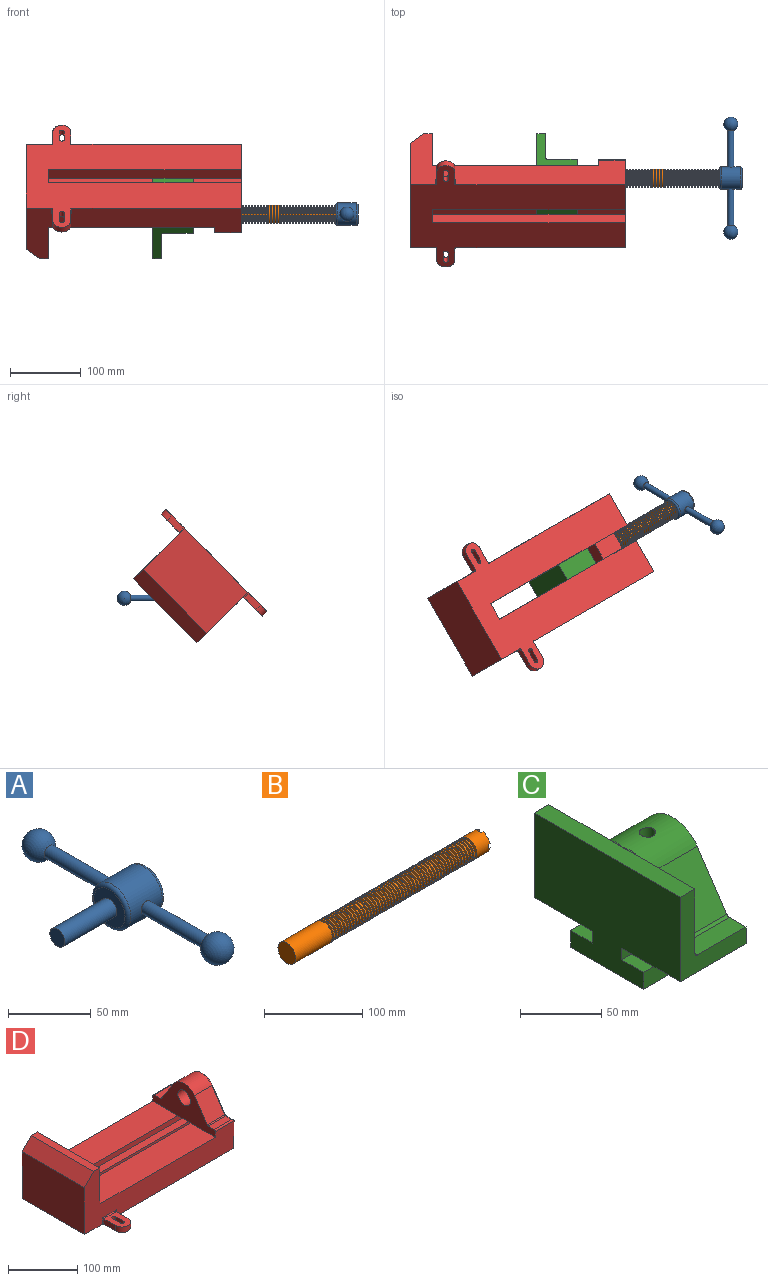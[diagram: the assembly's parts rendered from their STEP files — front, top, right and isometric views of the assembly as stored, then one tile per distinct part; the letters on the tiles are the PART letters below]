
ASSEMBLY  parts=4 mates=4
PART A: 11 faces, bbox 76.2x172.7x34.4 mm
  f0: sphere r=10.16mm, area 1231.8mm2, adj f1
  f1: cylinder r=4.45mm len=51.82mm, axis (0,1,0), area 1438.5mm2, adj f0,f4
  f2: sphere r=10.16mm, area 1231.8mm2, adj f3
  f3: cylinder r=4.45mm len=51.82mm, axis (0,1,0), area 1438.5mm2, adj f2,f4
  f4: cylinder r=15.88mm len=31.75mm, axis (-1,0,0), area 2534.7mm2, adj f1,f3,f9,f10
  f5: cylinder r=6.35mm len=44.45mm, axis (-1,0,0), area 1773.5mm2, adj f6,f8
  f6: plane 12.7x12.7mm, normal (-1,0,0), area 126.7mm2, adj f5
  f7: plane 26.67x26.67mm, normal (1,0,0), area 558.6mm2, adj f10
  f8: plane 26.67x26.67mm, normal (-1,0,0), area 432mm2, adj f5,f9
  f9: torus R=13.33mm, axis (1,0,0), area 374.8mm2, adj f4,f8
  f10: torus R=13.33mm, axis (1,0,0), area 374.8mm2, adj f4,f7
PART B: 220 faces, bbox 279.4x25.4x25.4 mm
  f0: cylinder r=12.7mm len=25.4mm, axis (-1,0,0), area 1468.2mm2, adj f1,f2,f3,f5,f7,f208,f209,f210
  f1: plane 9.9x9.9mm, normal (1,0,0), area 62.3mm2, adj f0,f4,f213,f216
  f2: plane 9.9x9.9mm, normal (1,0,0), area 62.3mm2, adj f0,f4,f210,f218
  f3: plane 9.9x9.9mm, normal (1,0,0), area 62.3mm2, adj f0,f4,f209,f212
  f4: cylinder r=6.35mm len=25.4mm, axis (1,0,0), area 960.3mm2, adj f1,f2,f3,f5,f6,f208,f209,f210
  f5: plane 9.9x9.9mm, normal (1,0,0), area 62.3mm2, adj f0,f4,f215,f217
  f6: plane 12.7x12.7mm, normal (1,0,0), area 126.7mm2, adj f4
  f7: cone r=12.7mm half-angle=76deg, axis (1,0,0), area 188mm2, adj f0,f9
  f8: cone r=10.16mm half-angle=76deg, axis (-1,0,0), area 188mm2, adj f9,f10
  f9: cylinder r=10.16mm len=20.32mm, axis (1,0,0), area 81.1mm2, adj f7,f8
  f10: cylinder r=12.7mm len=25.4mm, axis (-1,0,0), area 131.7mm2, adj f8,f11
  f11: cone r=12.7mm half-angle=76deg, axis (1,0,0), area 188mm2, adj f10,f13
  f12: cone r=10.16mm half-angle=76deg, axis (-1,0,0), area 188mm2, adj f13,f14
  f13: cylinder r=10.16mm len=20.32mm, axis (1,0,0), area 81.1mm2, adj f11,f12
  f14: cylinder r=12.7mm len=25.4mm, axis (-1,0,0), area 131.7mm2, adj f12,f15
  f15: cone r=12.7mm half-angle=76deg, axis (1,0,0), area 188mm2, adj f14,f17
  f16: cone r=10.16mm half-angle=76deg, axis (-1,0,0), area 188mm2, adj f17,f18
  f17: cylinder r=10.16mm len=20.32mm, axis (1,0,0), area 81.1mm2, adj f15,f16
  f18: cylinder r=12.7mm len=25.4mm, axis (-1,0,0), area 131.7mm2, adj f16,f19
  f19: cone r=12.7mm half-angle=76deg, axis (1,0,0), area 188mm2, adj f18,f21
  f20: cone r=10.16mm half-angle=76deg, axis (-1,0,0), area 188mm2, adj f21,f22
  f21: cylinder r=10.16mm len=20.32mm, axis (1,0,0), area 81.1mm2, adj f19,f20
  f22: cylinder r=12.7mm len=25.4mm, axis (-1,0,0), area 131.7mm2, adj f20,f23
  f23: cone r=12.7mm half-angle=76deg, axis (1,0,0), area 188mm2, adj f22,f25
  f24: cone r=10.16mm half-angle=76deg, axis (-1,0,0), area 188mm2, adj f25,f26
  f25: cylinder r=10.16mm len=20.32mm, axis (1,0,0), area 81.1mm2, adj f23,f24
  f26: cylinder r=12.7mm len=25.4mm, axis (-1,0,0), area 131.7mm2, adj f24,f27
  f27: cone r=12.7mm half-angle=76deg, axis (1,0,0), area 188mm2, adj f26,f29
  f28: cone r=10.16mm half-angle=76deg, axis (-1,0,0), area 188mm2, adj f29,f30
  f29: cylinder r=10.16mm len=20.32mm, axis (1,0,0), area 81.1mm2, adj f27,f28
  f30: cylinder r=12.7mm len=25.4mm, axis (-1,0,0), area 131.7mm2, adj f28,f31
  f31: cone r=12.7mm half-angle=76deg, axis (1,0,0), area 188mm2, adj f30,f33
  f32: cone r=10.16mm half-angle=76deg, axis (-1,0,0), area 188mm2, adj f33,f34
  f33: cylinder r=10.16mm len=20.32mm, axis (1,0,0), area 81.1mm2, adj f31,f32
  f34: cylinder r=12.7mm len=25.4mm, axis (-1,0,0), area 131.7mm2, adj f32,f35
  f35: cone r=12.7mm half-angle=76deg, axis (1,0,0), area 188mm2, adj f34,f37
  f36: cone r=10.16mm half-angle=76deg, axis (-1,0,0), area 188mm2, adj f37,f38
  f37: cylinder r=10.16mm len=20.32mm, axis (1,0,0), area 81.1mm2, adj f35,f36
  f38: cylinder r=12.7mm len=25.4mm, axis (-1,0,0), area 131.7mm2, adj f36,f39
  f39: cone r=12.7mm half-angle=76deg, axis (1,0,0), area 188mm2, adj f38,f41
  f40: cone r=10.16mm half-angle=76deg, axis (-1,0,0), area 188mm2, adj f41,f42
  f41: cylinder r=10.16mm len=20.32mm, axis (1,0,0), area 81.1mm2, adj f39,f40
  f42: cylinder r=12.7mm len=25.4mm, axis (-1,0,0), area 131.7mm2, adj f40,f43
  f43: cone r=12.7mm half-angle=76deg, axis (1,0,0), area 188mm2, adj f42,f45
  f44: cone r=10.16mm half-angle=76deg, axis (-1,0,0), area 188mm2, adj f45,f46
  f45: cylinder r=10.16mm len=20.32mm, axis (1,0,0), area 81.1mm2, adj f43,f44
  f46: cylinder r=12.7mm len=25.4mm, axis (-1,0,0), area 131.7mm2, adj f44,f47
  f47: cone r=12.7mm half-angle=76deg, axis (1,0,0), area 188mm2, adj f46,f49
  f48: cone r=10.16mm half-angle=76deg, axis (-1,0,0), area 188mm2, adj f49,f50
  f49: cylinder r=10.16mm len=20.32mm, axis (1,0,0), area 81.1mm2, adj f47,f48
  f50: cylinder r=12.7mm len=25.4mm, axis (-1,0,0), area 131.7mm2, adj f48,f51
  f51: cone r=12.7mm half-angle=76deg, axis (1,0,0), area 188mm2, adj f50,f53
  f52: cone r=10.16mm half-angle=76deg, axis (-1,0,0), area 188mm2, adj f53,f54
  f53: cylinder r=10.16mm len=20.32mm, axis (1,0,0), area 81.1mm2, adj f51,f52
  f54: cylinder r=12.7mm len=25.4mm, axis (-1,0,0), area 131.7mm2, adj f52,f55
  f55: cone r=12.7mm half-angle=76deg, axis (1,0,0), area 188mm2, adj f54,f57
  f56: cone r=10.16mm half-angle=76deg, axis (-1,0,0), area 188mm2, adj f57,f58
  f57: cylinder r=10.16mm len=20.32mm, axis (1,0,0), area 81.1mm2, adj f55,f56
  f58: cylinder r=12.7mm len=25.4mm, axis (-1,0,0), area 131.7mm2, adj f56,f59
  f59: cone r=12.7mm half-angle=76deg, axis (1,0,0), area 188mm2, adj f58,f61
  f60: cone r=10.16mm half-angle=76deg, axis (-1,0,0), area 188mm2, adj f61,f62
  f61: cylinder r=10.16mm len=20.32mm, axis (1,0,0), area 81.1mm2, adj f59,f60
  f62: cylinder r=12.7mm len=25.4mm, axis (-1,0,0), area 131.7mm2, adj f60,f63
  f63: cone r=12.7mm half-angle=76deg, axis (1,0,0), area 188mm2, adj f62,f65
  f64: cone r=10.16mm half-angle=76deg, axis (-1,0,0), area 188mm2, adj f65,f66
  f65: cylinder r=10.16mm len=20.32mm, axis (1,0,0), area 81.1mm2, adj f63,f64
  f66: cylinder r=12.7mm len=25.4mm, axis (-1,0,0), area 131.7mm2, adj f64,f67
  f67: cone r=12.7mm half-angle=76deg, axis (1,0,0), area 188mm2, adj f66,f69
  f68: cone r=10.16mm half-angle=76deg, axis (-1,0,0), area 188mm2, adj f69,f70
  f69: cylinder r=10.16mm len=20.32mm, axis (1,0,0), area 81.1mm2, adj f67,f68
  f70: cylinder r=12.7mm len=25.4mm, axis (-1,0,0), area 131.7mm2, adj f68,f71
  f71: cone r=12.7mm half-angle=76deg, axis (1,0,0), area 188mm2, adj f70,f73
  f72: cone r=10.16mm half-angle=76deg, axis (-1,0,0), area 188mm2, adj f73,f74
  f73: cylinder r=10.16mm len=20.32mm, axis (1,0,0), area 81.1mm2, adj f71,f72
  f74: cylinder r=12.7mm len=25.4mm, axis (-1,0,0), area 131.7mm2, adj f72,f75
  f75: cone r=12.7mm half-angle=76deg, axis (1,0,0), area 188mm2, adj f74,f77
  f76: cone r=10.16mm half-angle=76deg, axis (-1,0,0), area 188mm2, adj f77,f78
  f77: cylinder r=10.16mm len=20.32mm, axis (1,0,0), area 81.1mm2, adj f75,f76
  f78: cylinder r=12.7mm len=25.4mm, axis (-1,0,0), area 131.7mm2, adj f76,f79
  f79: cone r=12.7mm half-angle=76deg, axis (1,0,0), area 188mm2, adj f78,f81
  f80: cone r=10.16mm half-angle=76deg, axis (-1,0,0), area 188mm2, adj f81,f82
  f81: cylinder r=10.16mm len=20.32mm, axis (1,0,0), area 81.1mm2, adj f79,f80
  f82: cylinder r=12.7mm len=25.4mm, axis (-1,0,0), area 131.7mm2, adj f80,f83
  f83: cone r=12.7mm half-angle=76deg, axis (1,0,0), area 188mm2, adj f82,f85
  f84: cone r=10.16mm half-angle=76deg, axis (-1,0,0), area 188mm2, adj f85,f86
  f85: cylinder r=10.16mm len=20.32mm, axis (1,0,0), area 81.1mm2, adj f83,f84
  f86: cylinder r=12.7mm len=25.4mm, axis (-1,0,0), area 131.7mm2, adj f84,f87
  f87: cone r=12.7mm half-angle=76deg, axis (1,0,0), area 188mm2, adj f86,f89
  f88: cone r=10.16mm half-angle=76deg, axis (-1,0,0), area 188mm2, adj f89,f90
  f89: cylinder r=10.16mm len=20.32mm, axis (1,0,0), area 81.1mm2, adj f87,f88
  f90: cylinder r=12.7mm len=25.4mm, axis (-1,0,0), area 131.7mm2, adj f88,f91
  f91: cone r=12.7mm half-angle=76deg, axis (1,0,0), area 188mm2, adj f90,f93
  f92: cone r=10.16mm half-angle=76deg, axis (-1,0,0), area 188mm2, adj f93,f94
  f93: cylinder r=10.16mm len=20.32mm, axis (1,0,0), area 81.1mm2, adj f91,f92
  f94: cylinder r=12.7mm len=25.4mm, axis (-1,0,0), area 131.7mm2, adj f92,f95
  f95: cone r=12.7mm half-angle=76deg, axis (1,0,0), area 188mm2, adj f94,f97
  f96: cone r=10.16mm half-angle=76deg, axis (-1,0,0), area 188mm2, adj f97,f98
  f97: cylinder r=10.16mm len=20.32mm, axis (1,0,0), area 81.1mm2, adj f95,f96
  f98: cylinder r=12.7mm len=25.4mm, axis (-1,0,0), area 131.7mm2, adj f96,f99
  f99: cone r=12.7mm half-angle=76deg, axis (1,0,0), area 188mm2, adj f98,f101
  f100: cone r=10.16mm half-angle=76deg, axis (-1,0,0), area 188mm2, adj f101,f102
  f101: cylinder r=10.16mm len=20.32mm, axis (1,0,0), area 81.1mm2, adj f99,f100
  f102: cylinder r=12.7mm len=25.4mm, axis (-1,0,0), area 131.7mm2, adj f100,f103
  f103: cone r=12.7mm half-angle=76deg, axis (1,0,0), area 188mm2, adj f102,f105
  f104: cone r=10.16mm half-angle=76deg, axis (-1,0,0), area 188mm2, adj f105,f106
  f105: cylinder r=10.16mm len=20.32mm, axis (1,0,0), area 81.1mm2, adj f103,f104
  f106: cylinder r=12.7mm len=25.4mm, axis (-1,0,0), area 131.7mm2, adj f104,f107
  f107: cone r=12.7mm half-angle=76deg, axis (1,0,0), area 188mm2, adj f106,f109
  f108: cone r=10.16mm half-angle=76deg, axis (-1,0,0), area 188mm2, adj f109,f110
  f109: cylinder r=10.16mm len=20.32mm, axis (1,0,0), area 81.1mm2, adj f107,f108
  f110: cylinder r=12.7mm len=25.4mm, axis (-1,0,0), area 131.7mm2, adj f108,f111
  f111: cone r=12.7mm half-angle=76deg, axis (1,0,0), area 188mm2, adj f110,f113
  f112: cone r=10.16mm half-angle=76deg, axis (-1,0,0), area 188mm2, adj f113,f114
  f113: cylinder r=10.16mm len=20.32mm, axis (1,0,0), area 81.1mm2, adj f111,f112
  f114: cylinder r=12.7mm len=25.4mm, axis (-1,0,0), area 131.7mm2, adj f112,f115
  f115: cone r=12.7mm half-angle=76deg, axis (1,0,0), area 188mm2, adj f114,f117
  f116: cone r=10.16mm half-angle=76deg, axis (-1,0,0), area 188mm2, adj f117,f118
  f117: cylinder r=10.16mm len=20.32mm, axis (1,0,0), area 81.1mm2, adj f115,f116
  f118: cylinder r=12.7mm len=25.4mm, axis (-1,0,0), area 131.7mm2, adj f116,f119
  f119: cone r=12.7mm half-angle=76deg, axis (1,0,0), area 188mm2, adj f118,f121
  f120: cone r=10.16mm half-angle=76deg, axis (-1,0,0), area 188mm2, adj f121,f122
  f121: cylinder r=10.16mm len=20.32mm, axis (1,0,0), area 81.1mm2, adj f119,f120
  f122: cylinder r=12.7mm len=25.4mm, axis (-1,0,0), area 131.7mm2, adj f120,f123
  f123: cone r=12.7mm half-angle=76deg, axis (1,0,0), area 188mm2, adj f122,f125
  f124: cone r=10.16mm half-angle=76deg, axis (-1,0,0), area 188mm2, adj f125,f126
  f125: cylinder r=10.16mm len=20.32mm, axis (1,0,0), area 81.1mm2, adj f123,f124
  f126: cylinder r=12.7mm len=25.4mm, axis (-1,0,0), area 131.7mm2, adj f124,f127
  f127: cone r=12.7mm half-angle=76deg, axis (1,0,0), area 188mm2, adj f126,f129
  f128: cone r=10.16mm half-angle=76deg, axis (-1,0,0), area 188mm2, adj f129,f130
  f129: cylinder r=10.16mm len=20.32mm, axis (1,0,0), area 81.1mm2, adj f127,f128
  f130: cylinder r=12.7mm len=25.4mm, axis (-1,0,0), area 131.7mm2, adj f128,f131
  f131: cone r=12.7mm half-angle=76deg, axis (1,0,0), area 188mm2, adj f130,f133
  f132: cone r=10.16mm half-angle=76deg, axis (-1,0,0), area 188mm2, adj f133,f134
  f133: cylinder r=10.16mm len=20.32mm, axis (1,0,0), area 81.1mm2, adj f131,f132
  f134: cylinder r=12.7mm len=25.4mm, axis (-1,0,0), area 131.7mm2, adj f132,f135
  f135: cone r=12.7mm half-angle=76deg, axis (1,0,0), area 188mm2, adj f134,f137
  f136: cone r=10.16mm half-angle=76deg, axis (-1,0,0), area 188mm2, adj f137,f138
  f137: cylinder r=10.16mm len=20.32mm, axis (1,0,0), area 81.1mm2, adj f135,f136
  f138: cylinder r=12.7mm len=25.4mm, axis (-1,0,0), area 131.7mm2, adj f136,f139
  f139: cone r=12.7mm half-angle=76deg, axis (1,0,0), area 188mm2, adj f138,f141
  f140: cone r=10.16mm half-angle=76deg, axis (-1,0,0), area 188mm2, adj f141,f142
  f141: cylinder r=10.16mm len=20.32mm, axis (1,0,0), area 81.1mm2, adj f139,f140
  f142: cylinder r=12.7mm len=25.4mm, axis (-1,0,0), area 131.7mm2, adj f140,f143
  f143: cone r=12.7mm half-angle=76deg, axis (1,0,0), area 188mm2, adj f142,f145
  f144: cone r=10.16mm half-angle=76deg, axis (-1,0,0), area 188mm2, adj f145,f146
  f145: cylinder r=10.16mm len=20.32mm, axis (1,0,0), area 81.1mm2, adj f143,f144
  f146: cylinder r=12.7mm len=25.4mm, axis (-1,0,0), area 131.7mm2, adj f144,f147
  f147: cone r=12.7mm half-angle=76deg, axis (1,0,0), area 188mm2, adj f146,f149
  f148: cone r=10.16mm half-angle=76deg, axis (-1,0,0), area 188mm2, adj f149,f150
  f149: cylinder r=10.16mm len=20.32mm, axis (1,0,0), area 81.1mm2, adj f147,f148
  f150: cylinder r=12.7mm len=25.4mm, axis (-1,0,0), area 131.7mm2, adj f148,f151
  f151: cone r=12.7mm half-angle=76deg, axis (1,0,0), area 188mm2, adj f150,f153
  f152: cone r=10.16mm half-angle=76deg, axis (-1,0,0), area 188mm2, adj f153,f154
  f153: cylinder r=10.16mm len=20.32mm, axis (1,0,0), area 81.1mm2, adj f151,f152
  f154: cylinder r=12.7mm len=25.4mm, axis (-1,0,0), area 131.7mm2, adj f152,f155
  f155: cone r=12.7mm half-angle=76deg, axis (1,0,0), area 188mm2, adj f154,f157
  f156: cone r=10.16mm half-angle=76deg, axis (-1,0,0), area 188mm2, adj f157,f158
  f157: cylinder r=10.16mm len=20.32mm, axis (1,0,0), area 81.1mm2, adj f155,f156
  f158: cylinder r=12.7mm len=25.4mm, axis (-1,0,0), area 131.7mm2, adj f156,f159
  f159: cone r=12.7mm half-angle=76deg, axis (1,0,0), area 188mm2, adj f158,f161
  f160: cone r=10.16mm half-angle=76deg, axis (-1,0,0), area 188mm2, adj f161,f162
  f161: cylinder r=10.16mm len=20.32mm, axis (1,0,0), area 81.1mm2, adj f159,f160
  f162: cylinder r=12.7mm len=25.4mm, axis (-1,0,0), area 131.7mm2, adj f160,f163
  f163: cone r=12.7mm half-angle=76deg, axis (1,0,0), area 188mm2, adj f162,f165
  f164: cone r=10.16mm half-angle=76deg, axis (-1,0,0), area 188mm2, adj f165,f166
  f165: cylinder r=10.16mm len=20.32mm, axis (1,0,0), area 81.1mm2, adj f163,f164
  f166: cylinder r=12.7mm len=25.4mm, axis (-1,0,0), area 131.7mm2, adj f164,f167
  f167: cone r=12.7mm half-angle=76deg, axis (1,0,0), area 188mm2, adj f166,f169
  f168: cone r=10.16mm half-angle=76deg, axis (-1,0,0), area 188mm2, adj f169,f170
  f169: cylinder r=10.16mm len=20.32mm, axis (1,0,0), area 81.1mm2, adj f167,f168
  f170: cylinder r=12.7mm len=25.4mm, axis (-1,0,0), area 131.7mm2, adj f168,f171
  f171: cone r=12.7mm half-angle=76deg, axis (1,0,0), area 188mm2, adj f170,f173
  f172: cone r=10.16mm half-angle=76deg, axis (-1,0,0), area 188mm2, adj f173,f174
  f173: cylinder r=10.16mm len=20.32mm, axis (1,0,0), area 81.1mm2, adj f171,f172
  f174: cylinder r=12.7mm len=25.4mm, axis (-1,0,0), area 131.7mm2, adj f172,f175
  f175: cone r=12.7mm half-angle=76deg, axis (1,0,0), area 188mm2, adj f174,f177
  f176: cone r=10.16mm half-angle=76deg, axis (-1,0,0), area 188mm2, adj f177,f178
  f177: cylinder r=10.16mm len=20.32mm, axis (1,0,0), area 81.1mm2, adj f175,f176
  f178: cylinder r=12.7mm len=25.4mm, axis (-1,0,0), area 131.7mm2, adj f176,f179
  f179: cone r=12.7mm half-angle=76deg, axis (1,0,0), area 188mm2, adj f178,f181
  f180: cone r=10.16mm half-angle=76deg, axis (-1,0,0), area 188mm2, adj f181,f182
  f181: cylinder r=10.16mm len=20.32mm, axis (1,0,0), area 81.1mm2, adj f179,f180
  f182: cylinder r=12.7mm len=25.4mm, axis (-1,0,0), area 131.7mm2, adj f180,f183
  f183: cone r=12.7mm half-angle=76deg, axis (1,0,0), area 188mm2, adj f182,f185
  f184: cone r=10.16mm half-angle=76deg, axis (-1,0,0), area 188mm2, adj f185,f186
  f185: cylinder r=10.16mm len=20.32mm, axis (1,0,0), area 81.1mm2, adj f183,f184
  f186: cylinder r=12.7mm len=25.4mm, axis (-1,0,0), area 131.7mm2, adj f184,f187
  f187: cone r=12.7mm half-angle=76deg, axis (1,0,0), area 188mm2, adj f186,f189
  f188: cone r=10.16mm half-angle=76deg, axis (-1,0,0), area 188mm2, adj f189,f190
  f189: cylinder r=10.16mm len=20.32mm, axis (1,0,0), area 81.1mm2, adj f187,f188
  f190: cylinder r=12.7mm len=25.4mm, axis (-1,0,0), area 131.7mm2, adj f188,f191
  f191: cone r=12.7mm half-angle=76deg, axis (1,0,0), area 188mm2, adj f190,f193
  f192: cone r=10.16mm half-angle=76deg, axis (-1,0,0), area 188mm2, adj f193,f194
  f193: cylinder r=10.16mm len=20.32mm, axis (1,0,0), area 81.1mm2, adj f191,f192
  f194: cylinder r=12.7mm len=25.4mm, axis (-1,0,0), area 131.7mm2, adj f192,f195
  f195: cone r=12.7mm half-angle=76deg, axis (1,0,0), area 188mm2, adj f194,f197
  f196: cone r=10.16mm half-angle=76deg, axis (-1,0,0), area 188mm2, adj f197,f198
  f197: cylinder r=10.16mm len=20.32mm, axis (1,0,0), area 81.1mm2, adj f195,f196
  f198: cylinder r=12.7mm len=25.4mm, axis (-1,0,0), area 131.7mm2, adj f196,f199
  f199: cone r=12.7mm half-angle=76deg, axis (1,0,0), area 188mm2, adj f198,f201
  f200: cone r=10.16mm half-angle=76deg, axis (-1,0,0), area 188mm2, adj f201,f202
  f201: cylinder r=10.16mm len=20.32mm, axis (1,0,0), area 81.1mm2, adj f199,f200
  f202: cylinder r=12.7mm len=25.4mm, axis (-1,0,0), area 131.7mm2, adj f200,f203
  f203: cone r=12.7mm half-angle=76deg, axis (1,0,0), area 188mm2, adj f202,f205
  f204: cone r=10.16mm half-angle=76deg, axis (-1,0,0), area 188mm2, adj f205,f207
  f205: cylinder r=10.16mm len=20.32mm, axis (1,0,0), area 81.1mm2, adj f203,f204
  f206: plane 25.4x25.4mm, normal (-1,0,0), area 506.7mm2, adj f207
  f207: cylinder r=12.7mm len=52.45mm, axis (-1,0,0), area 4185.4mm2, adj f204,f206
  f208: plane 6.88x5.08mm, normal (1,0,0), area 32.7mm2, adj f0,f4,f209,f210
  f209: plane 6.62x2.54mm, normal (0,-1,0), area 16.8mm2, adj f0,f3,f4,f208
  f210: plane 6.62x2.54mm, normal (0,1,0), area 16.8mm2, adj f0,f2,f4,f208
  f211: plane 6.88x5.08mm, normal (1,0,0), area 32.7mm2, adj f0,f4,f212,f213
  f212: plane 6.62x2.54mm, normal (0,0,1), area 16.8mm2, adj f0,f3,f4,f211
  f213: plane 6.62x2.54mm, normal (0,0,-1), area 16.8mm2, adj f0,f1,f4,f211
  f214: plane 6.88x5.08mm, normal (1,0,0), area 32.7mm2, adj f0,f4,f215,f216
  f215: plane 6.62x2.54mm, normal (0,1,0), area 16.8mm2, adj f0,f4,f5,f214
  f216: plane 6.62x2.54mm, normal (0,-1,0), area 16.8mm2, adj f0,f1,f4,f214
  f217: plane 6.62x2.54mm, normal (0,0,-1), area 16.8mm2, adj f0,f4,f5,f219
  f218: plane 6.62x2.54mm, normal (0,0,1), area 16.8mm2, adj f0,f2,f4,f219
  f219: plane 6.88x5.08mm, normal (1,0,0), area 32.7mm2, adj f0,f4,f217,f218
PART C: 36 faces, bbox 57.2x127x89 mm
  f0: plane 57.15x50.8mm, normal (0,0,-1), area 2903.2mm2, adj f6,f9,f10,f23
  f1: cylinder r=12.7mm len=44.45mm, axis (1,0,0), area 3464.3mm2, adj f6,f15,f16
  f2: plane 41.91x14.52mm, normal (0,0,1), area 608.5mm2, adj f6,f11,f24,f25
  f3: plane 51.86x48.26mm, normal (1,0,0), area 1495.7mm2, adj f8,f10,f31,f33,f35
  f4: plane 51.86x48.26mm, normal (1,0,0), area 1495.7mm2, adj f8,f11,f24,f28,f29
  f5: plane 57.15x50.8mm, normal (0,0,-1), area 2903.2mm2, adj f6,f9,f11,f22
  f6: plane 127x85.09mm, normal (1,0,0), area 5190.6mm2, adj f0,f1,f2,f5,f7,f10,f11,f12
  f7: plane 41.91x14.52mm, normal (0,0,1), area 608.5mm2, adj f6,f10,f30,f31
  f8: plane 127x12.7mm, normal (0,0,1), area 1612.9mm2, adj f3,f4,f9,f10,f11,f26,f34
  f9: plane 127x85.09mm, normal (-1,0,0), area 9096.8mm2, adj f0,f5,f8,f10,f11,f17,f18,f19
  f10: plane 63.5x57.15mm, normal (0,-1,0), area 1372.3mm2, adj f0,f3,f6,f7,f8,f9,f31
  f11: plane 63.5x57.15mm, normal (0,1,0), area 1372.3mm2, adj f2,f4,f5,f6,f8,f9,f24
  f12: plane 41.91x38.43mm, normal (0,-0.83,0.56), area 1939.2mm2, adj f6,f13,f30,f33
  f13: cylinder r=25.4mm len=44.45mm, axis (1,0,0), area 2026.5mm2, adj f6,f12,f14,f16,f26,f28,f34,f35
  f14: plane 41.91x38.43mm, normal (0,0.83,0.56), area 1939.2mm2, adj f6,f13,f25,f29
  f15: plane 25.4x25.4mm, normal (1,0,0), area 506.7mm2, adj f1
  f16: cylinder r=5.08mm len=13.76mm, axis (0,0,1), area 414mm2, adj f1,f13
  f17: plane 57.15x19.05mm, normal (0,0,1), area 1088.7mm2, adj f6,f9,f18,f23
  f18: plane 57.15x12.7mm, normal (0,-1,0), area 725.8mm2, adj f6,f9,f17,f19
  f19: plane 63.5x57.15mm, normal (0,0,-1), area 3629mm2, adj f6,f9,f18,f20
  f20: plane 57.15x12.7mm, normal (0,1,0), area 725.8mm2, adj f6,f9,f19,f21
  f21: plane 57.15x19.05mm, normal (0,0,1), area 1088.7mm2, adj f6,f9,f20,f22
  f22: plane 57.15x8.89mm, normal (0,1,0), area 508.1mm2, adj f5,f6,f9,f21
  f23: plane 57.15x8.89mm, normal (0,-1,0), area 508.1mm2, adj f0,f6,f9,f17
  f24: cylinder r=2.54mm len=14.52mm, axis (0,-1,0), area 57.9mm2, adj f2,f4,f11,f27
  f25: cylinder r=2.54mm len=41.91mm, axis (1,0,0), area 104.3mm2, adj f2,f6,f14,f27
  f26: bspline ~12.24x2.8mm, area 20.9mm2, adj f8,f13,f28
  f27: sphere r=2.54mm, area 6.3mm2, adj f24,f25,f29
  f28: torus R=27.94mm, axis (1,0,0), area 57.8mm2, adj f4,f13,f26,f29
  f29: cylinder r=2.54mm len=39.84mm, axis (0,-0.56,0.83), area 184.6mm2, adj f4,f14,f27,f28
  f30: cylinder r=2.54mm len=41.91mm, axis (1,0,0), area 104.3mm2, adj f6,f7,f12,f32
  f31: cylinder r=2.54mm len=14.52mm, axis (0,-1,0), area 57.9mm2, adj f3,f7,f10,f32
  f32: sphere r=2.54mm, area 6.3mm2, adj f30,f31,f33
  f33: cylinder r=2.54mm len=39.84mm, axis (0,-0.56,-0.83), area 184.6mm2, adj f3,f12,f32,f35
  f34: bspline ~12.24x2.8mm, area 20.9mm2, adj f8,f13,f35
  f35: torus R=27.94mm, axis (1,0,0), area 57.8mm2, adj f3,f13,f33,f34
PART D: 61 faces, bbox 304.8x203.2x103.7 mm
  f0: plane 304.8x101.6mm, normal (0,1,0), area 13520.3mm2, adj f3,f4,f5,f6,f7,f8,f9,f16
  f1: plane 304.8x101.6mm, normal (0,-1,0), area 13520.3mm2, adj f2,f3,f5,f6,f7,f8,f9,f16
  f2: plane 234.95x50.8mm, normal (0,0,1), area 11935.5mm2, adj f1,f5,f16,f26
  f3: plane 127x99.06mm, normal (1,0,0), area 7097.5mm2, adj f0,f1,f9,f14,f17,f18,f19,f20
  f4: plane 234.95x50.8mm, normal (0,0,1), area 11935.5mm2, adj f0,f5,f16,f27
  f5: plane 127x101.6mm, normal (1,0,0), area 9516.1mm2, adj f0,f1,f2,f4,f6,f9,f18,f19
  f6: plane 127x12.7mm, normal (0,0,1), area 1612.9mm2, adj f0,f1,f5,f7
  f7: plane 127x19.05mm, normal (-0.71,0,0.71), area 3421.5mm2, adj f0,f1,f6,f8
  f8: plane 127x82.55mm, normal (-1,0,0), area 10483.8mm2, adj f0,f1,f7,f9
  f9: plane 304.8x203.2mm, normal (0,0,-1), area 33298.3mm2, adj f0,f1,f3,f5,f8,f21,f22,f39
  f10: plane 35.56x11.98mm, normal (0,0,1), area 426mm2, adj f16,f28,f29,f30
  f11: plane 38.43x35.56mm, normal (0,0.83,0.56), area 1645.4mm2, adj f12,f16,f29,f32
  f12: cylinder r=25.4mm len=42.19mm, axis (1,0,0), area 1770.2mm2, adj f11,f13,f16,f33
  f13: plane 38.43x35.56mm, normal (0,-0.83,0.56), area 1645.4mm2, adj f12,f16,f34,f35
  f14: cylinder r=12.7mm len=38.1mm, axis (1,0,0), area 3040.2mm2, adj f3,f16
  f15: plane 35.56x11.98mm, normal (0,0,1), area 426mm2, adj f16,f34,f36,f38
  f16: plane 127x63.5mm, normal (-1,0,0), area 4155.5mm2, adj f0,f1,f2,f4,f10,f11,f12,f13
  f17: plane 38.1x25.4mm, normal (0,0,-1), area 967.7mm2, adj f3,f16,f26,f27
  f18: plane 273.05x19.05mm, normal (0,0,-1), area 5201.6mm2, adj f3,f5,f19,f26
  f19: plane 273.05x12.7mm, normal (0,1,0), area 3467.7mm2, adj f3,f5,f18,f20
  f20: plane 273.05x19.05mm, normal (0,0,1), area 5201.6mm2, adj f3,f5,f19,f21
  f21: plane 273.05x16.51mm, normal (0,1,0), area 4508.1mm2, adj f3,f5,f9,f20
  f22: plane 273.05x16.51mm, normal (0,-1,0), area 4508.1mm2, adj f3,f5,f9,f23
  f23: plane 273.05x19.05mm, normal (0,0,1), area 5201.6mm2, adj f3,f5,f22,f24
  f24: plane 273.05x12.7mm, normal (0,-1,0), area 3467.7mm2, adj f3,f5,f23,f25
  f25: plane 273.05x19.05mm, normal (0,0,-1), area 5201.6mm2, adj f3,f5,f24,f27
  f26: plane 273.05x8.89mm, normal (0,1,0), area 2427.4mm2, adj f2,f3,f5,f17,f18
  f27: plane 273.05x8.89mm, normal (0,-1,0), area 2427.4mm2, adj f3,f4,f5,f17,f25
  f28: cylinder r=2.54mm len=38.1mm, axis (1,0,0), area 148.3mm2, adj f0,f10,f16,f30
  f29: cylinder r=2.54mm len=35.56mm, axis (-1,0,0), area 88.5mm2, adj f10,f11,f16,f31
  f30: cylinder r=2.54mm len=14.52mm, axis (0,1,0), area 54.3mm2, adj f3,f10,f28,f31
  f31: torus R=5.08mm, axis (-1,0,0), area 13.5mm2, adj f3,f29,f30,f32
  f32: cylinder r=2.54mm len=39.84mm, axis (0,0.56,-0.83), area 184.6mm2, adj f3,f11,f31,f33
  f33: torus R=22.86mm, axis (-1,0,0), area 191.4mm2, adj f3,f12,f32,f35
  f34: cylinder r=2.54mm len=35.56mm, axis (-1,0,0), area 88.5mm2, adj f13,f15,f16,f37
  f35: cylinder r=2.54mm len=39.84mm, axis (0,0.56,0.83), area 184.6mm2, adj f3,f13,f33,f37
  f36: cylinder r=2.54mm len=38.1mm, axis (-1,0,0), area 148.3mm2, adj f1,f15,f16,f38
  f37: torus R=5.08mm, axis (-1,0,0), area 13.5mm2, adj f3,f34,f35,f38
  f38: cylinder r=2.54mm len=14.52mm, axis (0,1,0), area 54.3mm2, adj f3,f15,f36,f37
  f39: plane 23.88x9.53mm, normal (-1,0,0), area 227.4mm2, adj f9,f45,f46,f60
  f40: plane 23.88x9.53mm, normal (1,0,0), area 227.4mm2, adj f9,f45,f46,f58
  f41: cylinder r=3.3mm len=9.53mm, axis (0,0,-1), area 98.8mm2, adj f9,f42,f44,f46
  f42: plane 15.62x9.53mm, normal (-1,0,0), area 148.8mm2, adj f9,f41,f43,f46
  f43: cylinder r=3.3mm len=9.53mm, axis (0,0,-1), area 98.8mm2, adj f9,f42,f44,f46
  f44: plane 15.62x9.53mm, normal (1,0,0), area 148.8mm2, adj f9,f41,f43,f46
  f45: cylinder r=12.7mm len=25.4mm, axis (0,0,-1), area 380mm2, adj f9,f39,f40,f46
  f46: plane 36.58x25.4mm, normal (0,0,1), area 722.4mm2, adj f39,f40,f41,f42,f43,f44,f45,f59
  f47: plane 23.88x9.53mm, normal (-1,0,0), area 227.4mm2, adj f9,f53,f54,f56
  f48: plane 23.88x9.53mm, normal (1,0,0), area 227.4mm2, adj f9,f53,f54,f55
  f49: cylinder r=3.3mm len=9.53mm, axis (0,0,-1), area 98.8mm2, adj f9,f50,f52,f54
  f50: plane 15.62x9.53mm, normal (-1,0,0), area 148.8mm2, adj f9,f49,f51,f54
  f51: cylinder r=3.3mm len=9.53mm, axis (0,0,-1), area 98.8mm2, adj f9,f50,f52,f54
  f52: plane 15.62x9.53mm, normal (1,0,0), area 148.8mm2, adj f9,f49,f51,f54
  f53: cylinder r=12.7mm len=25.4mm, axis (0,0,-1), area 380mm2, adj f9,f47,f48,f54
  f54: plane 36.58x25.4mm, normal (0,0,1), area 722.4mm2, adj f47,f48,f49,f50,f51,f52,f53,f57
  f55: cylinder r=1.52mm len=11.05mm, axis (0,0,-1), area 24.1mm2, adj f0,f9,f48,f57
  f56: cylinder r=1.52mm len=11.05mm, axis (0,0,1), area 24.1mm2, adj f0,f9,f47,f57
  f57: cylinder r=1.52mm len=28.45mm, axis (1,0,0), area 63.5mm2, adj f0,f54,f55,f56
  f58: cylinder r=1.52mm len=11.05mm, axis (0,0,1), area 24.1mm2, adj f1,f9,f40,f59
  f59: cylinder r=1.52mm len=28.45mm, axis (-1,0,0), area 63.5mm2, adj f1,f46,f58,f60
  f60: cylinder r=1.52mm len=11.05mm, axis (0,0,-1), area 24.1mm2, adj f1,f9,f39,f59
PLACE A t=(39.36,-63.99,89.91)mm
PLACE B t=(83.81,-63.99,89.91)mm
PLACE C rot(axis=(-1,0,0),134.7deg) t=(91.81,-118.12,219.74)mm
PLACE D rot(axis=(-1,0,0),134.7deg) t=(-55.84,-118.12,219.74)mm
MATE cylindrical B.f7 <-> D.f12  axis (-1,0,0) through (-124.09,-63.99,166.11)mm
MATE fastened A.f5 <-> B.f4  axis (-1,0,0) through (77.46,-63.99,166.11)mm
MATE revolute B.f7 <-> C.f28  axis (-1,0,0) through (-124.09,-63.99,166.11)mm
MATE planar C.f0 <-> D.f2  axis (0,-0.71,0.7) through (-152.66,-64.24,220)mm
